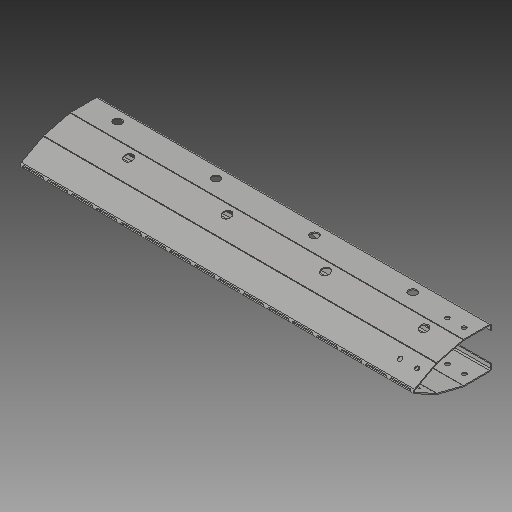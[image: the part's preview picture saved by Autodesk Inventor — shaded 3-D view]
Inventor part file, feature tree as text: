
AUTODESK INVENTOR PART (.ipt)
format: ipt  version: 2018 (Build 220112000, 112)  size: 888,832 bytes
history: native  units: mm
features: reference x25, other x24, sketch x23, hole x16, sheet_metal_op x13, plane x9, projected_geometry x7, extrude x4
ambient origin geometry x8: Origin, YZ Plane, XZ Plane, XY Plane, X Axis, Y Axis, Z Axis, Center Point
bodies: Solid1 (feature_tree)
feature tree (121):
  parser-record x4  (decoder bookkeeping rows leaked as tree rows — omitted from the tree; the rows remain in map.json)
  plane  "Work Plane1"
  sheet_metal_op  "Face1"
  plane  "Work Plane2"
  sheet_metal_op  "Face2"
  plane  "Work Plane3"
  sheet_metal_op  "Face3"
  plane  "Work Plane4"
  sheet_metal_op  "Face4"
  plane  "Work Plane5"
  sheet_metal_op  "Face5"
  plane  "Work Plane6"
  sheet_metal_op  "Face6"
  plane  "Work Plane7"
  sheet_metal_op  "Face7"
  other  "midtplan"
  extrude  "Extrusion3"  Depth=3.75mm
  extrude  "hulsæt til stifter"  Depth=3.0mm
  plane  "Work Plane11"
  sketch  "Sketch13"  dims[d18=1.5mm d19=6.0mm]
  plane  "Work Plane12"
  extrude  "balusterhul"  Depth=3.75mm
  extrude  "balusterhul skråkompensering"  Depth=3.0mm
  hole  "Hole2"  [1 undecoded]
  hole  "Hole4"  [1 undecoded]
  hole  "Hole6"  [1 undecoded]
  hole  "Hole8"  [1 undecoded]
  hole  "Hole10"  [1 undecoded]
  hole  "Hole12"  [1 undecoded]
  hole  "Hole14"  [1 undecoded]
  hole  "Hole16"  [1 undecoded]
  sketch  "Sketch1"  dims[d0=3.0mm d1=3.75mm]
  reference  "Reference1"
  reference  "Reference2"
  reference  "Reference3"
  reference  "Reference4"
  other  "Plate1"
  sketch  "Sketch2"  dims[d2=3.0mm d3=1.5mm]
  reference  "Reference5"
  reference  "Reference6"
  reference  "Reference7"
  reference  "Reference8"
  other  "Plate2"
  sheet_metal_op  "Bend1"
  sketch  "Sketch3"  dims[d4=6.0mm d5=3.75mm]
  reference  "Reference9"
  reference  "Reference10"
  reference  "Reference11"
  other  "Plate3"
  sheet_metal_op  "Bend2"
  sketch  "Sketch4"  dims[d6=3.75mm d7=3.0mm]
  reference  "Reference12"
  reference  "Reference13"
  reference  "Reference14"
  reference  "Reference15"
  other  "Plate4"
  sheet_metal_op  "Bend3"
  sketch  "Sketch5"  dims[d8=1.5mm d9=6.0mm]
  reference  "Reference16"
  reference  "Reference17"
  reference  "Reference18"
  other  "Plate5"
  sheet_metal_op  "Bend4"
  sketch  "Sketch6"  dims[d10=3.75mm d11=3.75mm]
  reference  "Reference19"
  reference  "Reference20"
  reference  "Reference21"
  other  "Plate6"
  sheet_metal_op  "Bend5"
  sketch  "Sketch7"  dims[d12=3.0mm d13=1.5mm]
  reference  "Reference22"
  reference  "Reference23"
  other  "Plate7"
  sheet_metal_op  "Bend6"
  sketch  "Sketch8"  dims[d14=6.0mm d15=3.75mm]
  reference  "Reference24"
  projected_geometry  "Projected Loop1"
  other  "huller til stifter"
  projected_geometry  "Projected Loop3"
  sketch  "Sketch12"  dims[d16=3.75mm d17=3.0mm]
  projected_geometry  "Projected Loop4"
  reference  "Reference25"
  sketch  "Sketch14"  dims[d20=3.75mm d21=3.75mm]
  sketch  "Sketch15"  dims[d22=3.0mm d23=1.5mm]
  projected_geometry  "Projected Loop5"
  projected_geometry  "Projected Loop6"
  sketch  "Sketch16"  dims[d24=6.0mm d25=3.75mm]
  projected_geometry  "Projected Loop7"
  projected_geometry  "Projected Loop8"
  sketch  "Sketch17"  dims[d26=3.75mm d27=3.0mm]
  sketch  "Sketch18"  dims[d28=1.5mm d29=6.0mm]
  hole  "Hole1"  [1 undecoded]
  sketch  "Sketch19"  dims[d30=3.75mm d31=3.0mm]
  hole  "Hole3"  [1 undecoded]
  sketch  "Sketch20"  dims[d32=0.0mm d33=3.0mm]
  hole  "Hole5"  [1 undecoded]
  sketch  "Sketch21"  dims[d39=250.0mm d41=33.7mm]
  hole  "Hole7"  [1 undecoded]
  sketch  "Sketch22"  dims[d42=33.7mm d43=60.0mm d44=60.0mm]
  hole  "Hole9"  [1 undecoded]
  sketch  "Sketch23"  dims[d45=16.85mm d46=65.0mm]
  hole  "Hole11"  [1 undecoded]
  sketch  "Sketch24"  dims[d47=60.0mm]
  hole  "Hole13"  [1 undecoded]
  sketch  "Sketch25"  dims[d48=10.0mm d49=0.0mm]
  hole  "Hole15"  [1 undecoded]
  sketch  "Sketch26"  dims[d68=291.052mm d69=10.0mm d70=0.0mm d73=96.672mm d77=39.001254mm d78=26.6mm d79=25.8mm d80=40.0mm d82=302.737mm d83=10.0mm d85=10.0mm d87=302.737mm d88=113.655385mm d89=56.827692mm d90=90.0deg d91=90.0deg d92=49.5mm d93=100.0mm d94=0.0mm d97=2.046461mm d98=1.023231mm d99=10.0mm d100=0.0mm d101=90.0mm d102=30.0mm d103=522.678194mm d104=342.992513mm d106=342.992513mm d107=30.0mm d108=30.0mm d109=342.992513mm d110=30.0mm d111=342.992513mm d112=624.299345mm d113=10.0mm d114=3.0mm d115=0.0mm d116=221.306832mm d117=119.685681mm d118=96.672222mm d119=61.97046mm d120=1208.948mm d121=8.0mm d122=62.8mm d123=6.0mm d124=170.0mm d126=75.36mm d127=10.0mm d129=10.0mm d131=3.0mm d132=0.0mm d133=12.56mm d134=13.5mm d135=6.0mm d136=4.0mm d137=2.0mm d138=90.0deg d139=8.0mm d140=0.0mm d141=13.5mm d142=6.0mm d143=4.0mm d144=2.0mm d145=90.0deg d146=8.0mm d147=0.0mm d148=13.5mm d149=6.0mm d150=4.0mm d151=2.0mm d152=90.0deg d153=8.0mm d154=0.0mm d155=13.5mm d156=6.0mm d157=4.0mm d158=2.0mm d159=90.0deg d160=8.0mm d161=0.0mm d162=13.5mm d163=6.0mm d164=4.0mm d165=2.0mm d166=90.0deg d167=8.0mm d168=0.0mm d169=13.5mm d170=6.0mm d171=4.0mm d172=2.0mm d173=90.0deg d174=8.0mm d175=0.0mm d176=13.5mm d177=6.0mm d178=4.0mm d179=2.0mm d180=90.0deg d181=8.0mm d182=0.0mm d183=13.5mm d184=6.0mm d185=4.0mm d186=2.0mm d187=90.0deg d188=8.0mm d189=0.0mm d190=1.0mm d191=1.0mm d192=140.0mm d193=3.0mm d194=0.0mm]
  other  "Cut1"
  other  "plantehuller"
  other  "bukkeperforering"
  other  "test af laskehuller"
  other  "modul.iam"
  other  "model:1"
  other  "Definition1"
  other  "søjle+vange.iam"
  other  "modul top:1"
  other  "vange top:1"
  other  "modul top.iam"
note: 16 required parameter values undecoded (feature->parameter linkage not recoverable at this tier; creation-order binding heuristic only, values carry confidence <= 0.55)
note: 4 file-system paths scrubbed to <path> (originals preserved in map.json)
